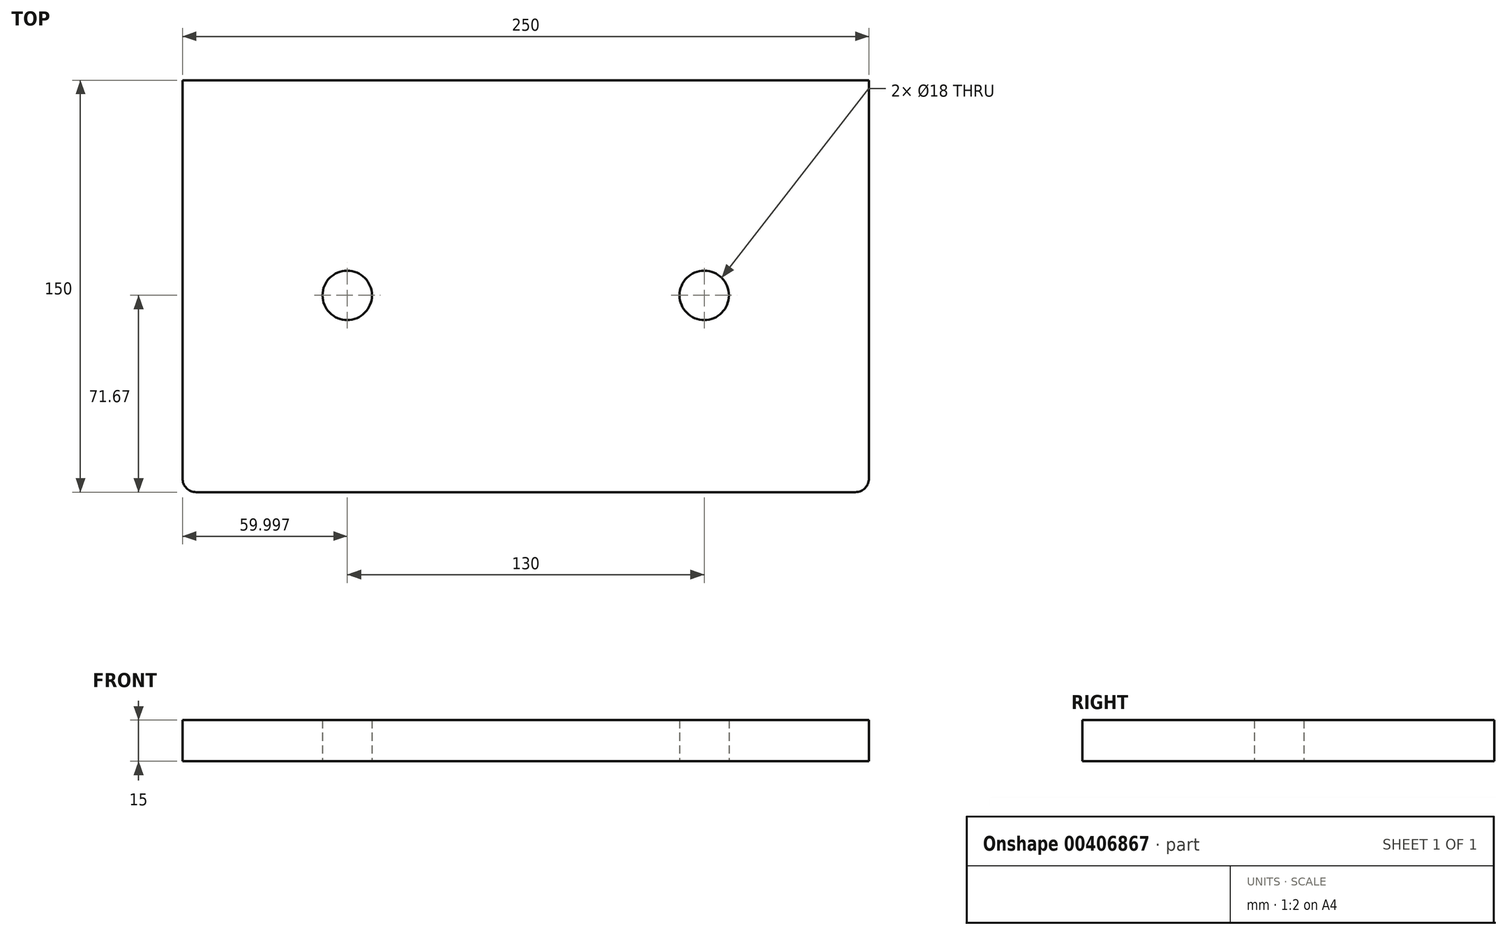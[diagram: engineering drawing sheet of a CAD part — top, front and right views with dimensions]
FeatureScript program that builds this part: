
annotation { "Feature Type Name" : "Feature", "Feature Type Description" : "" }
export const myFeature = defineFeature(function(context is Context, id is Id, definition is map)
    precondition{}
    {
        {
            var Q0;
            Q0=qCreatedBy(makeId("Top.planeOp"),FACE);
            var sketch = newSketch(context, id + "F0", { "sketchPlane" : qUnion([Q0])});
            skLineSegment(sketch, "E0.bottom", {"start": v(-124.2, 78.33) * mm, "end": v(125.8, 78.33) * mm});
            skLineSegment(sketch, "E0.top", {"start": v(-119.2, -71.67) * mm, "end": v(120.8, -71.67) * mm});
            skLineSegment(sketch, "E0.left", {"start": v(-124.2, 78.33) * mm, "end": v(-124.2, -66.67) * mm});
            skLineSegment(sketch, "E0.right", {"start": v(125.8, 78.33) * mm, "end": v(125.8, -66.67) * mm});
            skCircle(sketch, "E1", {"center": v(-64.2, 0) * mm, "radius": 9 * mm});
            skCircle(sketch, "E2", {"center": v(65.8, 0) * mm, "radius": 9 * mm});
            skPoint(sketch, "E3.visualSharp", {"position": v(-124.2, -71.67) * mm});
            skArc(sketch, "E3.filletArc", {"start": v(-124.2, -66.67) * mm, "mid": v(-122.73, -70.2) * mm, "end": v(-119.2, -71.67) * mm});
            skPoint(sketch, "E4.visualSharp", {"position": v(125.8, -71.67) * mm});
            skArc(sketch, "E4.filletArc", {"start": v(120.8, -71.67) * mm, "mid": v(124.34, -70.2) * mm, "end": v(125.8, -66.67) * mm});
            skSolve(sketch);
        }
        {
            var Q0;
            Q0 = qSketchRegion(id + "F0", true);
            extrude(context, id + "F1", {"entities" : qUnion([Q0]), "depth" : 15 * mm});
        }
    });
